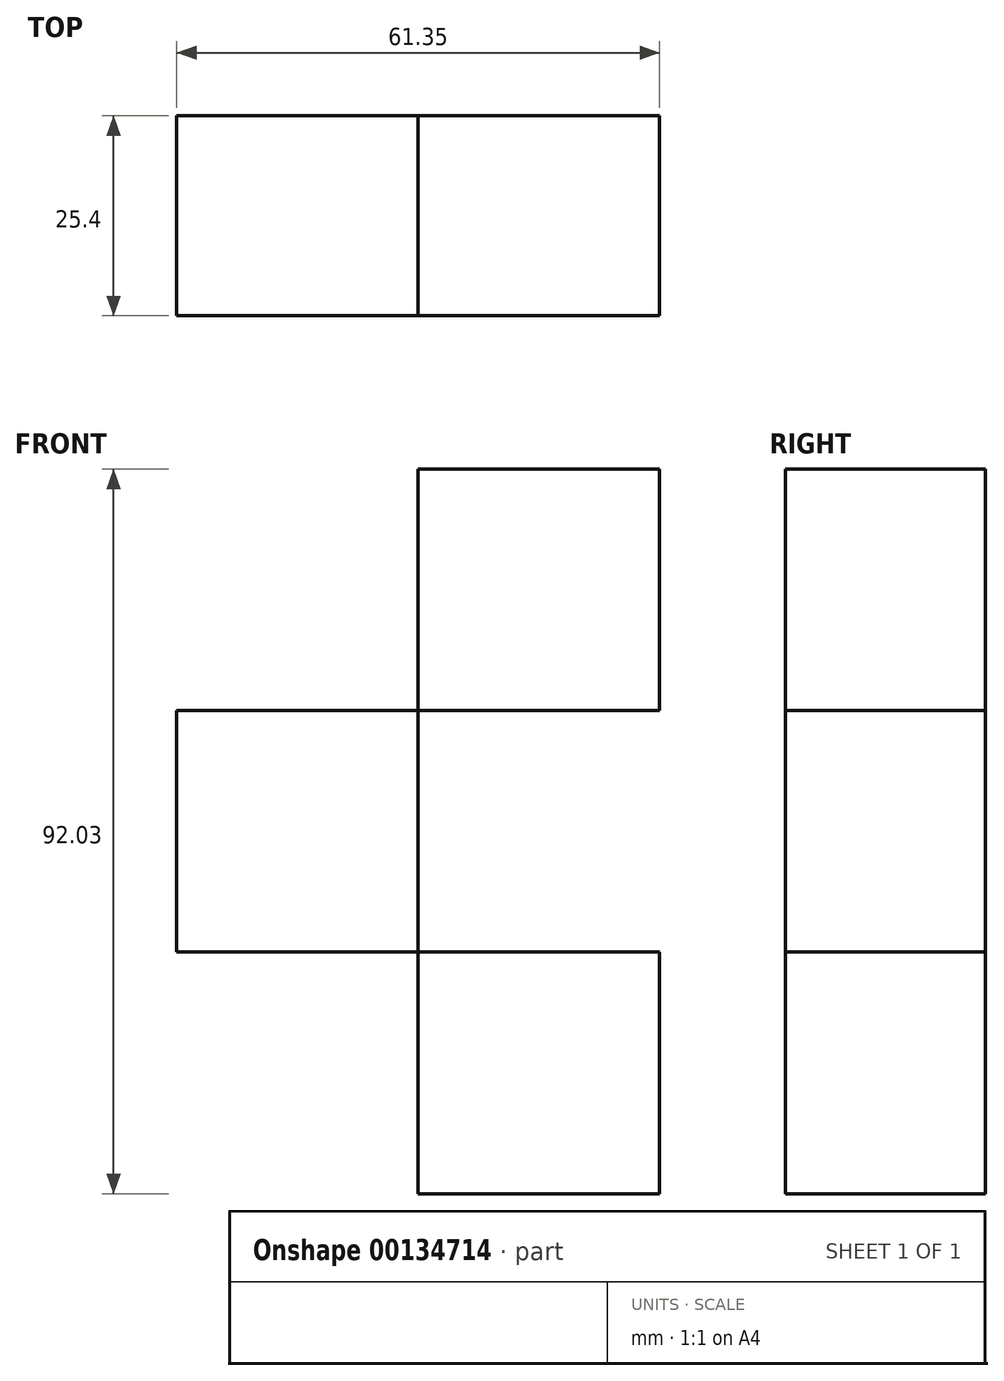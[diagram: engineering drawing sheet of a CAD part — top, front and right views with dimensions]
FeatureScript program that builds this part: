
annotation { "Feature Type Name" : "Feature", "Feature Type Description" : "" }
export const myFeature = defineFeature(function(context is Context, id is Id, definition is map)
    precondition{}
    {
        {
            var Q0;
            Q0=qCreatedBy(makeId("Front.planeOp"),FACE);
            var sketch = newSketch(context, id + "F0", { "sketchPlane" : qUnion([Q0])});
            skLineSegment(sketch, "E0", {"start": v(-30.68, 69.57) * mm, "end": v(-30.68, 38.9) * mm});
            skLineSegment(sketch, "E1", {"start": v(-30.68, 38.9) * mm, "end": v(-61.35, 38.9) * mm});
            skLineSegment(sketch, "E2", {"start": v(-61.35, 38.9) * mm, "end": v(-61.35, 8.22) * mm});
            skLineSegment(sketch, "E3", {"start": v(-61.35, 8.22) * mm, "end": v(-30.68, 8.22) * mm});
            skLineSegment(sketch, "E4", {"start": v(-30.68, 8.22) * mm, "end": v(-30.68, -22.46) * mm});
            skLineSegment(sketch, "E5", {"start": v(-30.68, -22.46) * mm, "end": v(0, -22.46) * mm});
            skLineSegment(sketch, "E6", {"start": v(0, -22.46) * mm, "end": v(0, 8.22) * mm});
            skLineSegment(sketch, "E7", {"start": v(-30.68, 69.57) * mm, "end": v(0, 69.57) * mm});
            skLineSegment(sketch, "E8", {"start": v(0, 69.57) * mm, "end": v(0, 38.9) * mm});
            skLineSegment(sketch, "E9", {"start": v(0, 38.9) * mm, "end": v(-30.68, 38.9) * mm});
            skLineSegment(sketch, "E10", {"start": v(-30.68, 38.9) * mm, "end": v(-30.68, 8.22) * mm});
            skLineSegment(sketch, "E11", {"start": v(-30.68, 8.22) * mm, "end": v(0, 8.22) * mm});
            skSolve(sketch);
        }
        {
            var Q0;
            Q0=makeQuery(id+"F0.imprint","IMPRINT",FACE,{"disambiguationData":[TD([[makeQuery(id+"F0.imprint","IMPRINT",EDGE,{"derivedFrom":sQuery(id+"F0.wireOp",EDGE,"E1")}),1.0]])]});
            var Q1;
            Q1=makeQuery(id+"F0.imprint","IMPRINT",FACE,{"disambiguationData":[TD([[makeQuery(id+"F0.imprint","IMPRINT",EDGE,{"derivedFrom":sQuery(id+"F0.wireOp",EDGE,"E0")}),1.0]])]});
            var Q2;
            Q2=makeQuery(id+"F0.imprint","IMPRINT",FACE,{"disambiguationData":[TD([[makeQuery(id+"F0.imprint","IMPRINT",EDGE,{"derivedFrom":sQuery(id+"F0.wireOp",EDGE,"E4")}),1.0]])]});
            extrude(context, id + "F1", {"entities" : qUnion([Q0, Q1, Q2]), "depth" : 25.4 * mm});
        }
    });
